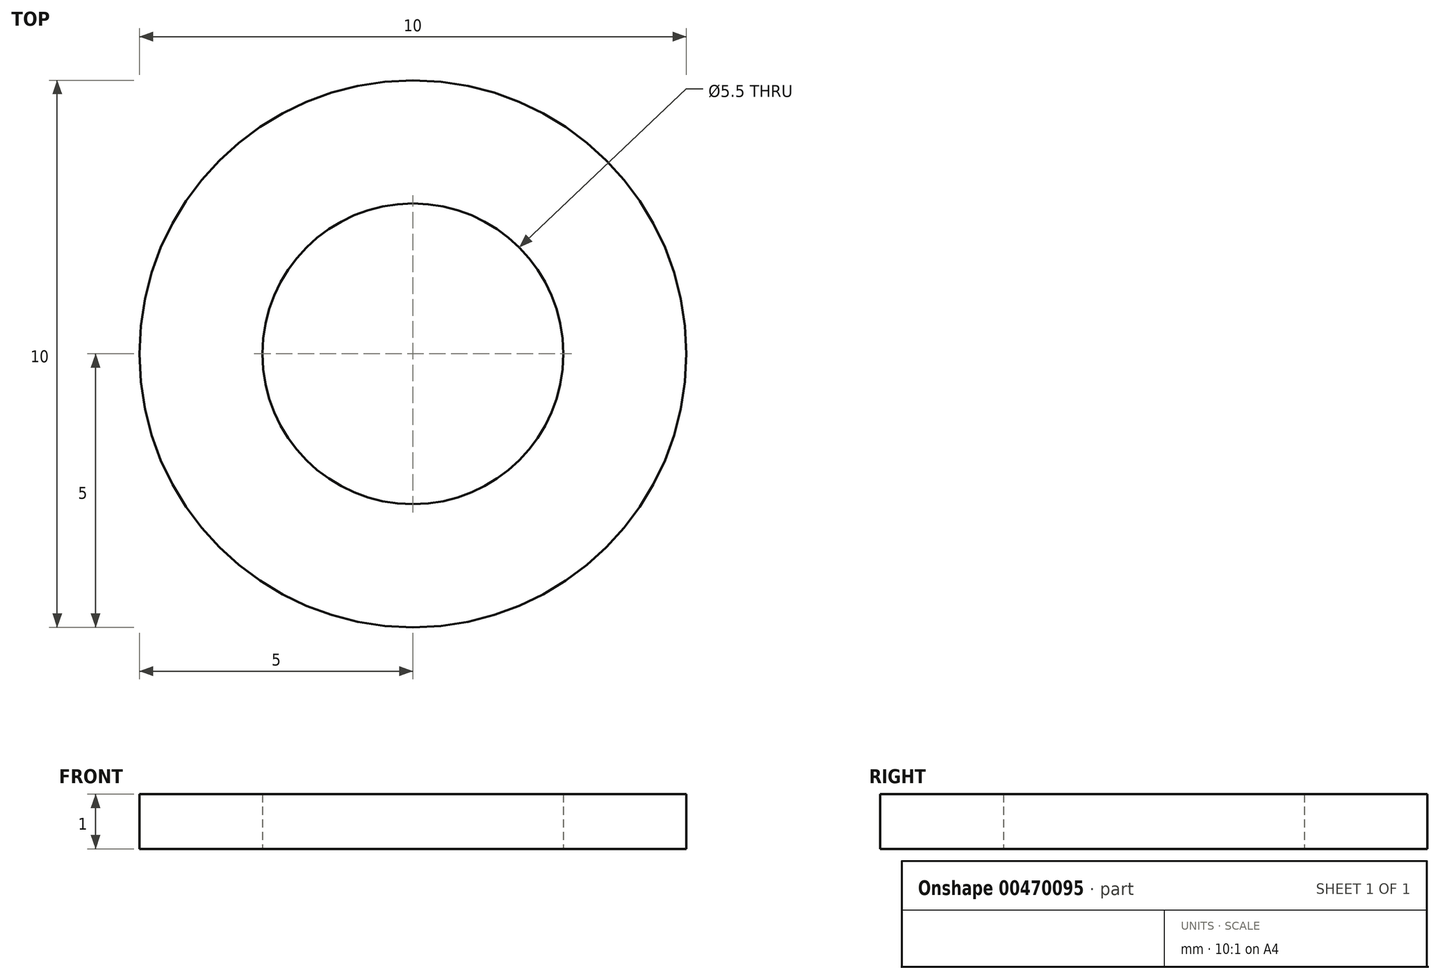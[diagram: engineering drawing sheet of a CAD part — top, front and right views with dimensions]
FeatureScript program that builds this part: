
annotation { "Feature Type Name" : "Feature", "Feature Type Description" : "" }
export const myFeature = defineFeature(function(context is Context, id is Id, definition is map)
    precondition{}
    {
        {
            var Q0;
            Q0=qCreatedBy(makeId("Top.planeOp"),FACE);
            var sketch = newSketch(context, id + "F0", { "sketchPlane" : qUnion([Q0])});
            skCircle(sketch, "E0", {"center": v(0, 0) * mm, "radius": 5 * mm});
            skCircle(sketch, "E1", {"center": v(0, 0) * mm, "radius": 2.75 * mm});
            skSolve(sketch);
        }
        {
            var Q0;
            Q0=makeQuery(id+"F0.imprint","IMPRINT",FACE,{"disambiguationData":[TD([[makeQuery(id+"F0.imprint","IMPRINT",EDGE,{"derivedFrom":sQuery(id+"F0.wireOp",EDGE,"E0")}),1.0]])]});
            extrude(context, id + "F1", {"entities" : qUnion([Q0]), "depth" : 1 * mm});
        }
    });
